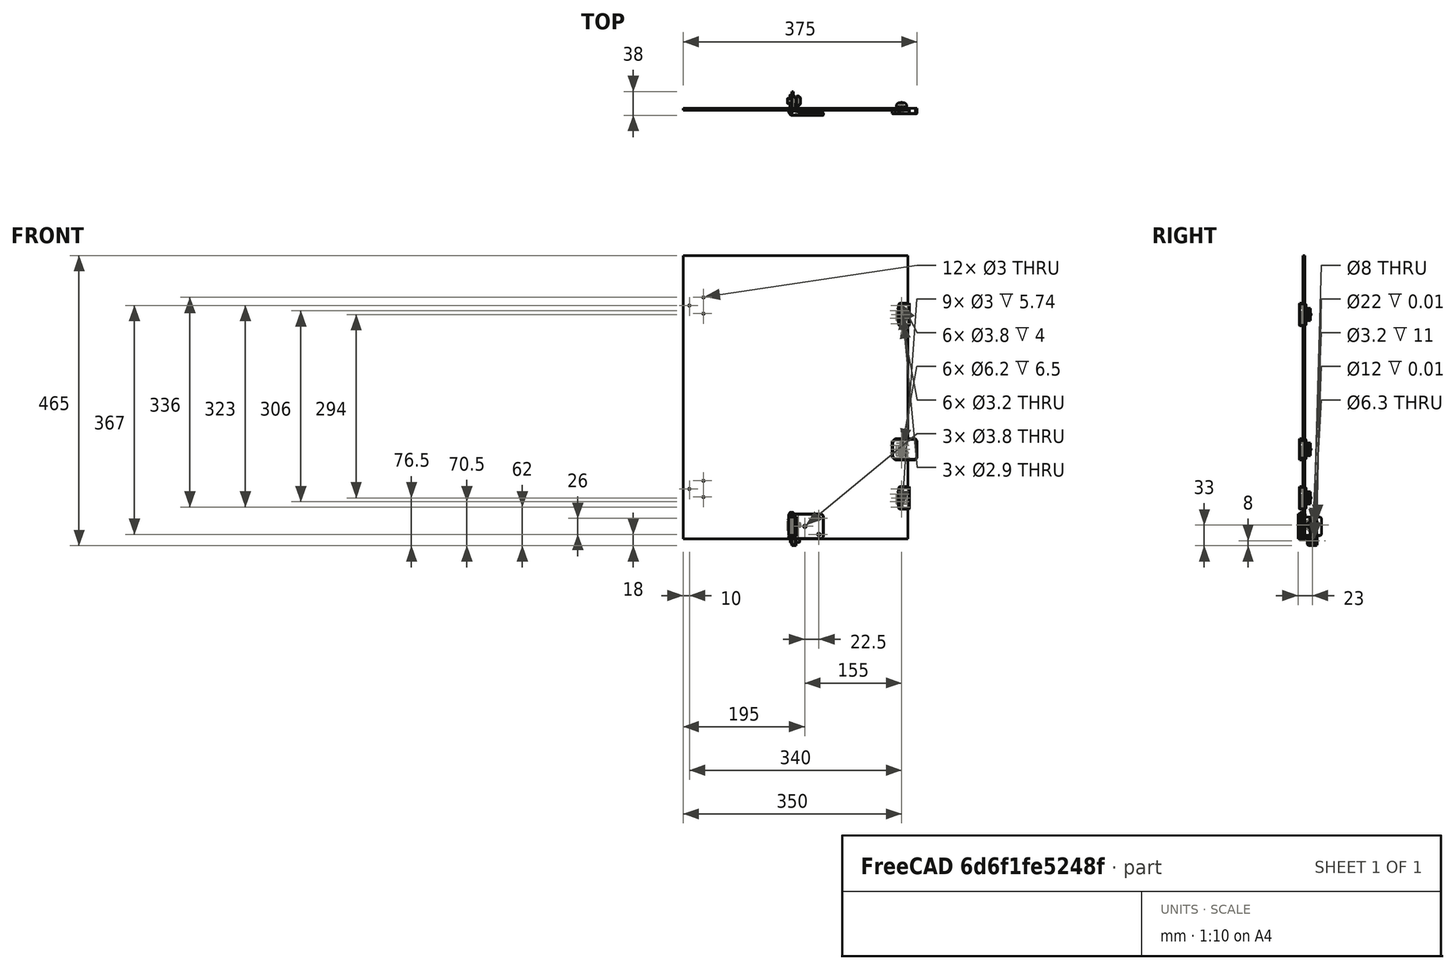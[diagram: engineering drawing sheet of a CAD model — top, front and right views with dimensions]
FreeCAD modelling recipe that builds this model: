
FCSTD DOCUMENT  (FreeCAD 0.19R24291 (Git))
Label: front-panel-assembly
License: All rights reserved
LicenseURL: http://en.wikipedia.org/wiki/All_rights_reserved
objects: Part::FeaturePython×43, Part::Feature×17, Part::Cylinder×6, App::Part×4, Part::Box×3, PartDesign::CoordinateSystem×1
note: 70 computed .brp shape members not serialized (recipe doc carries the construction recipe); baked Part::Feature solids carry a one-line shape summary decoded from their .brp

FEATURE [Part::FeaturePython] Screw101  label="M6x12-Screw001"  # Fasteners workbench fastener (typed FeaturePython)
  Placement = pos=(-5,15,-3) rot=(0,-1,0;1.5708rad)
  diameter = 4
  invert = false
  leftHanded = false
  length = 1
  lengthCustom = 12
  matchOuter = true
  offset = 0
  thread = false
  type = 39
FEATURE [Part::FeaturePython] HeatSet012  label="M3x3-HeatSet003"  # WARN: FeaturePython — macro-defined, semantics opaque (R4)
  Placement = pos=(170,0,130) rot=(-1,0,0;1.5708rad)
  baseObject = -> Chamfer016016008004017002013001 [Edge47]
  diameter = 2
  invert = false
  leftHanded = false
  offset = 0
FEATURE [Part::FeaturePython] Screw089  label="M3x6-Screw033"  # Fasteners workbench fastener (typed FeaturePython)
  Placement = pos=(170,3.55,80) rot=(-1,0,0;1.5708rad)
  baseObject = -> Washer009 [Edge1]
  diameter = 1
  invert = false
  leftHanded = false
  length = 0
  lengthCustom = 6
  matchOuter = true
  offset = 0
  thread = false
  type = 39
FEATURE [Part::FeaturePython] Washer012  label="M3-Washer031"  # Fasteners workbench fastener (typed FeaturePython)
  Placement = pos=(170,3,130) rot=(-1,0,0;1.5708rad)
  baseObject = -> Chamfer016016008004017002013001 [Edge47]
  diameter = 4
  invert = false
  leftHanded = false
  matchOuter = true
  offset = 3
  type = 5
FEATURE [Part::FeaturePython] Washer011  label="M3-Washer032"  # Fasteners workbench fastener (typed FeaturePython)
  Placement = pos=(170,3,157) rot=(-1,0,0;1.5708rad)
  baseObject = -> Chamfer016016008004017002013001 [Edge52]
  diameter = 4
  invert = false
  leftHanded = false
  matchOuter = true
  offset = 3
  type = 5
FEATURE [Part::FeaturePython] Washer010  label="M3-Washer030"  # Fasteners workbench fastener (typed FeaturePython)
  Placement = pos=(170,3,51) rot=(-1,0,0;1.5708rad)
  baseObject = -> Chamfer016016008004017002013005001 [Edge25]
  diameter = 4
  invert = false
  leftHanded = false
  matchOuter = true
  offset = 3
  type = 5
FEATURE [Part::FeaturePython] Washer009  label="M3-Washer029"  # Fasteners workbench fastener (typed FeaturePython)
  Placement = pos=(170,3,80) rot=(-1,0,0;1.5708rad)
  baseObject = -> Chamfer016016008004017002013005001 [Edge30]
  diameter = 4
  invert = false
  leftHanded = false
  matchOuter = true
  offset = 3
  type = 5
FEATURE [Part::FeaturePython] Washer008  label="M3-Washer022"  # Fasteners workbench fastener (typed FeaturePython)
  Placement = pos=(170,3,345) rot=(-1,0,0;1.5708rad)
  baseObject = -> Chamfer016016008004017002013005002 [Edge25]
  diameter = 4
  invert = false
  leftHanded = false
  matchOuter = true
  offset = 3
  type = 5
FEATURE [Part::Feature] Cut010011008009001  label="frame-magnet-mount002"
  Placement = pos=(170,4,55.5) rot=(0,0,1;0rad)
  shape: bbox 16 x 7.5 x 20 mm, 17 faces (baked)
FEATURE [Part::FeaturePython] HeatSet  label="M3x3-HeatSet"  # WARN: FeaturePython — macro-defined, semantics opaque (R4)
  Placement = pos=(15,-8,20) rot=(1,0,0;1.5708rad)
  baseObject = -> Chamfer006006010001 [Edge11]
  diameter = 2
  invert = true
  leftHanded = false
  offset = 0
FEATURE [Part::Feature] Chamfer016016008004017002013005006  label="knob001"
  shape: bbox 8 x 19 x 19 mm, 35 faces (baked)
FEATURE [Part::FeaturePython] HeatSet006  label="M3x4-HeatSet005"  # WARN: FeaturePython — macro-defined, semantics opaque (R4)
  Placement = pos=(37.5,-8,33) rot=(1,0,0;1.5708rad)
  baseObject = -> Chamfer016016008004017002013005004 [Edge13]
  diameter = 2
  invert = true
  leftHanded = false
  offset = 0
FEATURE [PartDesign::CoordinateSystem] LCS_front_panel  label="LCS_front-panel"
  AttacherType = Attacher::AttachEngine3D
FEATURE [Part::Box] Box008  label="19x5x1p5m-magnet002"
  AttacherType = Attacher::AttachEngine3D
  Height = 19
  Length = 5
  Placement = pos=(167.5,-1.5,350) rot=(0,0,1;0rad)
  Width = 1.5
FEATURE [Part::FeaturePython] Screw107  label="M3x8-Screw045"  # Fasteners workbench fastener (typed FeaturePython)
  Placement = pos=(170,5,359.5) rot=(1,0,0;1.5708rad)
  baseObject = -> Cut010011008009003016005 [Edge25]
  diameter = 6
  invert = true
  leftHanded = false
  length = 5
  lengthCustom = 8
  matchOuter = true
  offset = 7
  thread = false
  type = 30
FEATURE [Part::Cylinder] Cylinder003  label="6x3-magnet003"
  Angle = 360
  AttacherType = Attacher::AttachEngine3D
  Height = 3
  Placement = pos=(170,9,149.5) rot=(-1,0,0;1.5708rad)
  Radius = 3
FEATURE [Part::Cylinder] Cylinder002  label="6x3-magnet002"
  Angle = 360
  AttacherType = Attacher::AttachEngine3D
  Height = 3
  Placement = pos=(170,9,137.5) rot=(-1,0,0;1.5708rad)
  Radius = 3
FEATURE [Part::FeaturePython] HeatSet015  label="M3x3-HeatSet007"  # WARN: FeaturePython — macro-defined, semantics opaque (R4)
  Placement = pos=(170,0,374) rot=(-1,0,0;1.5708rad)
  baseObject = -> Chamfer016016008004017002013005002 [Edge30]
  diameter = 2
  invert = false
  leftHanded = false
  offset = 0
FEATURE [Part::Cylinder] Cylinder001  label="6x3-magnet001"
  Angle = 360
  AttacherType = Attacher::AttachEngine3D
  Height = 3
  Placement = pos=(170,9,71.5) rot=(-1,0,0;1.5708rad)
  Radius = 3
FEATURE [Part::FeaturePython] HeatSet004  label="M3x4-HeatSet001"  # WARN: FeaturePython — macro-defined, semantics opaque (R4)
  Placement = pos=(8,15,22) rot=(0,1,0;1.5708rad)
  baseObject = -> Chamfer006006020001 [Edge21]
  diameter = 2
  invert = true
  leftHanded = false
  offset = 0
FEATURE [Part::FeaturePython] HeatSet005  label="M3x4-HeatSet006"  # WARN: FeaturePython — macro-defined, semantics opaque (R4)
  Placement = pos=(15,-8,20) rot=(1,0,0;1.5708rad)
  baseObject = -> Chamfer016016008004017002013005004 [Edge11]
  diameter = 2
  invert = true
  leftHanded = false
  offset = 0
FEATURE [Part::Feature] Chamfer016016008004017002013005005  label="side-hinge001"
  Placement = pos=(0,0,5) rot=(0,0,1;0rad)
  shape: bbox 16 x 36 x 30 mm, 60 faces (baked)
FEATURE [Part::Cylinder] Cylinder004  label="6x3-magnet004"
  Angle = 360
  AttacherType = Attacher::AttachEngine3D
  Height = 3
  Placement = pos=(170,9,353.5) rot=(-1,0,0;1.5708rad)
  Radius = 3
FEATURE [Part::Cylinder] Cylinder005  label="6x3-magnet005"
  Angle = 360
  AttacherType = Attacher::AttachEngine3D
  Height = 3
  Placement = pos=(170,9,365.5) rot=(-1,0,0;1.5708rad)
  Radius = 3
FEATURE [Part::Box] Box006  label="19x5x1p5m-magnet"
  AttacherType = Attacher::AttachEngine3D
  Height = 19
  Length = 5
  Placement = pos=(167.5,-1.5,56.5) rot=(0,0,1;0rad)
  Width = 1.5
FEATURE [Part::Feature] Chamfer016016008004017002013005004  label="front-hinge001"
  shape: bbox 56 x 12 x 40 mm, 51 faces (baked)
FEATURE [Part::Box] Box007  label="19x5x1p5m-magnet001"
  AttacherType = Attacher::AttachEngine3D
  Height = 19
  Length = 5
  Placement = pos=(167.5,-1.5,134) rot=(0,0,1;0rad)
  Width = 1.5
FEATURE [Part::FeaturePython] Screw100  label="M3x40-Screw001"  # Fasteners workbench fastener (typed FeaturePython)
  Placement = pos=(-6,-1,39.6) rot=(0,0,1;0rad)
  baseObject = -> Chamfer016016008004017002013005004 [Edge71]
  diameter = 4
  invert = false
  leftHanded = false
  length = 10
  lengthCustom = 40
  matchOuter = true
  offset = 0
  thread = false
  type = 33
FEATURE [Part::FeaturePython] HeatSet011  label="M3x3-HeatSet004"  # WARN: FeaturePython — macro-defined, semantics opaque (R4)
  Placement = pos=(170,0,80) rot=(-1,0,0;1.5708rad)
  baseObject = -> Chamfer016016008004017002013005001 [Edge30]
  diameter = 2
  invert = false
  leftHanded = false
  offset = 0
FEATURE [Part::FeaturePython] HeatSet010  label="M3x3-HeatSet005"  # WARN: FeaturePython — macro-defined, semantics opaque (R4)
  Placement = pos=(170,0,51) rot=(-1,0,0;1.5708rad)
  baseObject = -> Chamfer016016008004017002013005001 [Edge25]
  diameter = 2
  invert = false
  leftHanded = false
  offset = 0
FEATURE [Part::FeaturePython] HeatSet009  label="M3x4-HeatSet002"  # WARN: FeaturePython — macro-defined, semantics opaque (R4)
  Placement = pos=(8,15,22) rot=(0,1,0;1.5708rad)
  baseObject = -> Chamfer016016008004017002013005003 [Edge21]
  diameter = 2
  invert = true
  leftHanded = false
  offset = 0
FEATURE [Part::FeaturePython] HeatSet008  label="M3x4-HeatSet003"  # WARN: FeaturePython — macro-defined, semantics opaque (R4)
  Placement = pos=(-6,-1,0) rot=(1,0,0;3.14159rad)
  baseObject = -> Chamfer016016008004017002013005004 [Edge91]
  diameter = 2
  invert = true
  leftHanded = false
  offset = 0
FEATURE [Part::FeaturePython] HeatSet007  label="M3x4-HeatSet004"  # WARN: FeaturePython — macro-defined, semantics opaque (R4)
  Placement = pos=(37.5,-8,7) rot=(1,0,0;1.5708rad)
  baseObject = -> Chamfer016016008004017002013005004 [Edge12]
  diameter = 2
  invert = true
  leftHanded = false
  offset = 0
FEATURE [Part::FeaturePython] Screw085  label="M3x6-Screw026"  # Fasteners workbench fastener (typed FeaturePython)
  Placement = pos=(170,3.55,374) rot=(-1,0,0;1.5708rad)
  baseObject = -> Washer [Edge1]
  diameter = 1
  invert = false
  leftHanded = false
  length = 0
  lengthCustom = 6
  matchOuter = true
  offset = 0
  thread = false
  type = 39
FEATURE [Part::FeaturePython] Screw086  label="M3x6-Screw"  # Fasteners workbench fastener (typed FeaturePython)
  Placement = pos=(170,3.55,345) rot=(-1,0,0;1.5708rad)
  baseObject = -> Washer008 [Edge1]
  diameter = 1
  invert = false
  leftHanded = false
  length = 0
  lengthCustom = 6
  matchOuter = true
  offset = 0
  thread = false
  type = 39
FEATURE [Part::FeaturePython] Screw087  label="M3x6-Screw036"  # Fasteners workbench fastener (typed FeaturePython)
  Placement = pos=(170,3.55,157) rot=(-1,0,0;1.5708rad)
  baseObject = -> Washer011 [Edge1]
  diameter = 1
  invert = false
  leftHanded = false
  length = 0
  lengthCustom = 6
  matchOuter = true
  offset = 0
  thread = false
  type = 39
FEATURE [Part::FeaturePython] Screw088  label="M3x6-Screw035"  # Fasteners workbench fastener (typed FeaturePython)
  Placement = pos=(170,3.55,130) rot=(-1,0,0;1.5708rad)
  baseObject = -> Washer012 [Edge1]
  diameter = 1
  invert = false
  leftHanded = false
  length = 0
  lengthCustom = 6
  matchOuter = true
  offset = 0
  thread = false
  type = 39
FEATURE [Part::FeaturePython] Screw109  label="M3x8-Screw044"  # Fasteners workbench fastener (typed FeaturePython)
  Placement = pos=(170,5,65.5) rot=(1,0,0;1.5708rad)
  baseObject = -> Cut010011008009001 [Edge25]
  diameter = 6
  invert = true
  leftHanded = false
  length = 5
  lengthCustom = 8
  matchOuter = true
  offset = 7
  thread = false
  type = 30
FEATURE [Part::FeaturePython] HeatSet002  label="M3x3-HeatSet002"  # WARN: FeaturePython — macro-defined, semantics opaque (R4)
  Placement = pos=(37.5,-8,33) rot=(1,0,0;1.5708rad)
  baseObject = -> Chamfer006006010001 [Edge13]
  diameter = 2
  invert = true
  leftHanded = false
  offset = 0
FEATURE [Part::FeaturePython] Screw099  label="M3x16-Screw001"  # Fasteners workbench fastener (typed FeaturePython)
  Placement = pos=(-10,15,22) rot=(0,-1,0;1.5708rad)
  baseObject = -> Chamfer016016008004017002013005006 [Edge61]
  diameter = 4
  invert = true
  leftHanded = false
  length = 6
  lengthCustom = 16
  matchOuter = true
  offset = 0
  thread = false
  type = 33
FEATURE [Part::Cylinder] Cylinder  label="6x3-magnet"
  Angle = 360
  AttacherType = Attacher::AttachEngine3D
  Height = 3
  Placement = pos=(170,9,59.5) rot=(-1,0,0;1.5708rad)
  Radius = 3
FEATURE [Part::FeaturePython] Washer  label="M3-Washer"  # Fasteners workbench fastener (typed FeaturePython)
  Placement = pos=(170,3,374) rot=(-1,0,0;1.5708rad)
  baseObject = -> Chamfer016016008004017002013005002 [Edge30]
  diameter = 4
  invert = false
  leftHanded = false
  matchOuter = true
  offset = 3
  type = 5
FEATURE [Part::Feature] Chamfer016016008004017002013005002  label="door-magnet-mount-small001"
  Placement = pos=(185,4,341.5) rot=(0,0,1;0rad)
  shape: bbox 18 x 9 x 36 mm, 29 faces (baked)
FEATURE [Part::Feature] Chamfer016016008004017002013005001  label="door-magnet-mount-small"
  Placement = pos=(185,4,47.5) rot=(0,0,1;0rad)
  shape: bbox 18 x 9 x 36 mm, 29 faces (baked)
FEATURE [Part::Feature] Chamfer016016008004017002013001  label="door-magnet-mount-large"
  Placement = pos=(185,4,126.5) rot=(0,0,1;0rad)
  shape: bbox 40 x 9 x 34 mm, 29 faces (baked)
FEATURE [Part::Feature] Cut010011008009003016004  label="frame-magnet-mount"
  Placement = pos=(170,4,133.5) rot=(0,0,1;0rad)
  shape: bbox 16 x 7.5 x 20 mm, 17 faces (baked)
FEATURE [Part::FeaturePython] Screw090  label="M3x6-Screw034"  # Fasteners workbench fastener (typed FeaturePython)
  Placement = pos=(170,3.55,51) rot=(-1,0,0;1.5708rad)
  baseObject = -> Washer010 [Edge1]
  diameter = 1
  invert = false
  leftHanded = false
  length = 0
  lengthCustom = 6
  matchOuter = true
  offset = 0
  thread = false
  type = 39
FEATURE [Part::Feature] Chamfer006006020001  label="nut001"
  shape: bbox 16 x 16 x 12 mm, 35 faces (baked)
FEATURE [Part::Feature] Cut002004005004001  label="hinge-support001"
  shape: bbox 7 x 16 x 16 mm, 30 faces (baked)
FEATURE [Part::FeaturePython] HeatSet013  label="M3x3-HeatSet006"  # WARN: FeaturePython — macro-defined, semantics opaque (R4)
  Placement = pos=(170,0,157) rot=(-1,0,0;1.5708rad)
  baseObject = -> Chamfer016016008004017002013001 [Edge52]
  diameter = 2
  invert = false
  leftHanded = false
  offset = 0
FEATURE [Part::FeaturePython] Screw108  label="M3x8-Screw"  # Fasteners workbench fastener (typed FeaturePython)
  Placement = pos=(170,5,143.5) rot=(1,0,0;1.5708rad)
  baseObject = -> Cut010011008009003016004 [Edge25]
  diameter = 6
  invert = true
  leftHanded = false
  length = 5
  lengthCustom = 8
  matchOuter = true
  offset = 7
  thread = false
  type = 30
FEATURE [Part::FeaturePython] HeatSet014  label="M3x3-HeatSet008"  # WARN: FeaturePython — macro-defined, semantics opaque (R4)
  Placement = pos=(170,0,345) rot=(-1,0,0;1.5708rad)
  baseObject = -> Chamfer016016008004017002013005002 [Edge25]
  diameter = 2
  invert = false
  leftHanded = false
  offset = 0
FEATURE [Part::FeaturePython] Screw102  label="M3x6-Screw025"  # Fasteners workbench fastener (typed FeaturePython)
  Placement = pos=(37.5,-2,33) rot=(-1,0,0;1.5708rad)
  baseObject = -> Chamfer016016008004017002013005004 [Edge98]
  diameter = 1
  invert = false
  leftHanded = false
  length = 0
  lengthCustom = 6
  matchOuter = true
  offset = 2
  thread = false
  type = 39
FEATURE [Part::FeaturePython] HeatSet003  label="M3x4-HeatSet"  # WARN: FeaturePython — macro-defined, semantics opaque (R4)
  Placement = pos=(-6,-1,0) rot=(1,0,0;3.14159rad)
  baseObject = -> Chamfer006006010001 [Edge91]
  diameter = 2
  invert = true
  leftHanded = false
  offset = 0
FEATURE [Part::FeaturePython] HeatSet001  label="M3x3-HeatSet001"  # WARN: FeaturePython — macro-defined, semantics opaque (R4)
  Placement = pos=(37.5,-8,7) rot=(1,0,0;1.5708rad)
  baseObject = -> Chamfer006006010001 [Edge12]
  diameter = 2
  invert = true
  leftHanded = false
  offset = 0
FEATURE [Part::Feature] Chamfer006006010001  label="front-hinge"
  shape: bbox 56 x 12 x 40 mm, 51 faces (baked)
FEATURE [Part::FeaturePython] Screw091  label="M3x6-Screw003"  # Fasteners workbench fastener (typed FeaturePython)
  Placement = pos=(37.5,-2,7) rot=(-1,0,0;1.5708rad)
  baseObject = -> Chamfer006006010001 [Edge96]
  diameter = 1
  invert = false
  leftHanded = false
  length = 0
  lengthCustom = 6
  matchOuter = true
  offset = 2
  thread = false
  type = 39
FEATURE [Part::FeaturePython] Screw092  label="M3x6-Screw004"  # Fasteners workbench fastener (typed FeaturePython)
  Placement = pos=(15,-2,20) rot=(-1,0,0;1.5708rad)
  baseObject = -> Chamfer006006010001 [Edge94]
  diameter = 1
  invert = false
  leftHanded = false
  length = 0
  lengthCustom = 6
  matchOuter = true
  offset = 2
  thread = false
  type = 39
FEATURE [Part::FeaturePython] Screw094  label="M3x40-Screw"  # Fasteners workbench fastener (typed FeaturePython)
  Placement = pos=(-6,-1,39.6) rot=(0,0,1;0rad)
  baseObject = -> Chamfer006006010001 [Edge71]
  diameter = 4
  invert = false
  leftHanded = false
  length = 10
  lengthCustom = 40
  matchOuter = true
  offset = 0
  thread = false
  type = 33
FEATURE [Part::FeaturePython] Screw095  label="M6x12-Screw"  # Fasteners workbench fastener (typed FeaturePython)
  Placement = pos=(-5,15,-3) rot=(0,-1,0;1.5708rad)
  diameter = 4
  invert = false
  leftHanded = false
  length = 1
  lengthCustom = 12
  matchOuter = true
  offset = 0
  thread = false
  type = 39
FEATURE [Part::FeaturePython] Screw096  label="M3x6-Screw022"  # Fasteners workbench fastener (typed FeaturePython)
  Placement = pos=(37.5,-2,33) rot=(-1,0,0;1.5708rad)
  baseObject = -> Chamfer006006010001 [Edge98]
  diameter = 1
  invert = false
  leftHanded = false
  length = 0
  lengthCustom = 6
  matchOuter = true
  offset = 2
  thread = false
  type = 39
FEATURE [Part::Feature] Chamfer006006019001  label="side-hinge"
  Placement = pos=(0,0,5) rot=(0,0,1;0rad)
  shape: bbox 16 x 36 x 30 mm, 60 faces (baked)
FEATURE [Part::Feature] Chamfer006006016001  label="knob"
  shape: bbox 8 x 19 x 19 mm, 35 faces (baked)
FEATURE [Part::FeaturePython] Screw093  label="M3x16-Screw"  # Fasteners workbench fastener (typed FeaturePython)
  Placement = pos=(-10,15,22) rot=(0,-1,0;1.5708rad)
  baseObject = -> Chamfer006006016001 [Edge61]
  diameter = 4
  invert = true
  leftHanded = false
  length = 6
  lengthCustom = 16
  matchOuter = true
  offset = 0
  thread = false
  type = 33
FEATURE [App::Part] Part048  label="door-hinge"
  Group = -> [Chamfer006006019001,Screw093,Chamfer006006016001,Screw095,Screw092,Screw091,Screw096,Screw094,Chamfer006006010001,Chamfer006006020001,Cut002004005004001,HeatSet,HeatSet001,HeatSet002,HeatSet003,HeatSet004]
  Origin = -> Origin048
  Placement = pos=(0,-30,354) rot=(0,0,1;0rad)
FEATURE [Part::Feature] Chamfer016016008004017002013005003  label="nut"
  shape: bbox 16 x 16 x 12 mm, 35 faces (baked)
FEATURE [Part::Feature] Cut008004003004014002002005003004003002003001003001002001002002003003  label="hinge-support"
  shape: bbox 7 x 16 x 16 mm, 30 faces (baked)
FEATURE [Part::FeaturePython] Screw097  label="M3x6-Screw023"  # Fasteners workbench fastener (typed FeaturePython)
  Placement = pos=(37.5,-2,7) rot=(-1,0,0;1.5708rad)
  baseObject = -> Chamfer016016008004017002013005004 [Edge96]
  diameter = 1
  invert = false
  leftHanded = false
  length = 0
  lengthCustom = 6
  matchOuter = true
  offset = 2
  thread = false
  type = 39
FEATURE [Part::FeaturePython] Screw098  label="M3x6-Screw024"  # Fasteners workbench fastener (typed FeaturePython)
  Placement = pos=(15,-2,20) rot=(-1,0,0;1.5708rad)
  baseObject = -> Chamfer016016008004017002013005004 [Edge94]
  diameter = 1
  invert = false
  leftHanded = false
  length = 0
  lengthCustom = 6
  matchOuter = true
  offset = 2
  thread = false
  type = 39
FEATURE [App::Part] Part049  label="door-hinge001"
  Group = -> [Chamfer016016008004017002013005005,Screw099,Chamfer016016008004017002013005006,Screw101,Screw098,Screw097,Screw102,Screw100,Chamfer016016008004017002013005004,Chamfer016016008004017002013005003,Cut008004003004014002002005003004003002003001003001002001002002003003,HeatSet009,HeatSet008,HeatSet007,HeatSet006,HeatSet005]
  Origin = -> Origin049
  Placement = pos=(0,-30,60) rot=(0,0,1;0rad)
FEATURE [Part::Feature] Cut010011008009003016005  label="frame-magnet-mount001"
  Placement = pos=(170,4,349.5) rot=(0,0,1;0rad)
  shape: bbox 16 x 7.5 x 20 mm, 17 faces (baked)
FEATURE [Part::Feature] Cut008004003004014002002005003004003002003001003001002001002002003004  label="panel-360x454x3mm"
  Placement = pos=(-185,34,0) rot=(0,0,1;0rad)
  shape: bbox 360 x 3 x 454 mm, 18 faces (baked)
FEATURE [App::Part] Part047  label="door-panel"
  Group = -> [Cut010011008009001,Cut010011008009003016004,Cut010011008009003016005,Chamfer016016008004017002013001,Chamfer016016008004017002013005001,Chamfer016016008004017002013005002,Washer008,Washer,Washer010,Washer009,Washer012,Washer011,Screw086,Screw085,Screw088,Screw087,Screw090,Screw089,HeatSet012,HeatSet011,HeatSet010,HeatSet013,HeatSet015,HeatSet014,Cylinder,Cylinder001,Cylinder002,Cylinder003,+9 more]
  Origin = -> Origin047
  Placement = pos=(185,-34,0) rot=(0,0,1;0rad)
FEATURE [App::Part] Part046  label="front-panel"
  Group = -> [Part047,Part049,Part048,LCS_front_panel]
  Origin = -> Origin046
